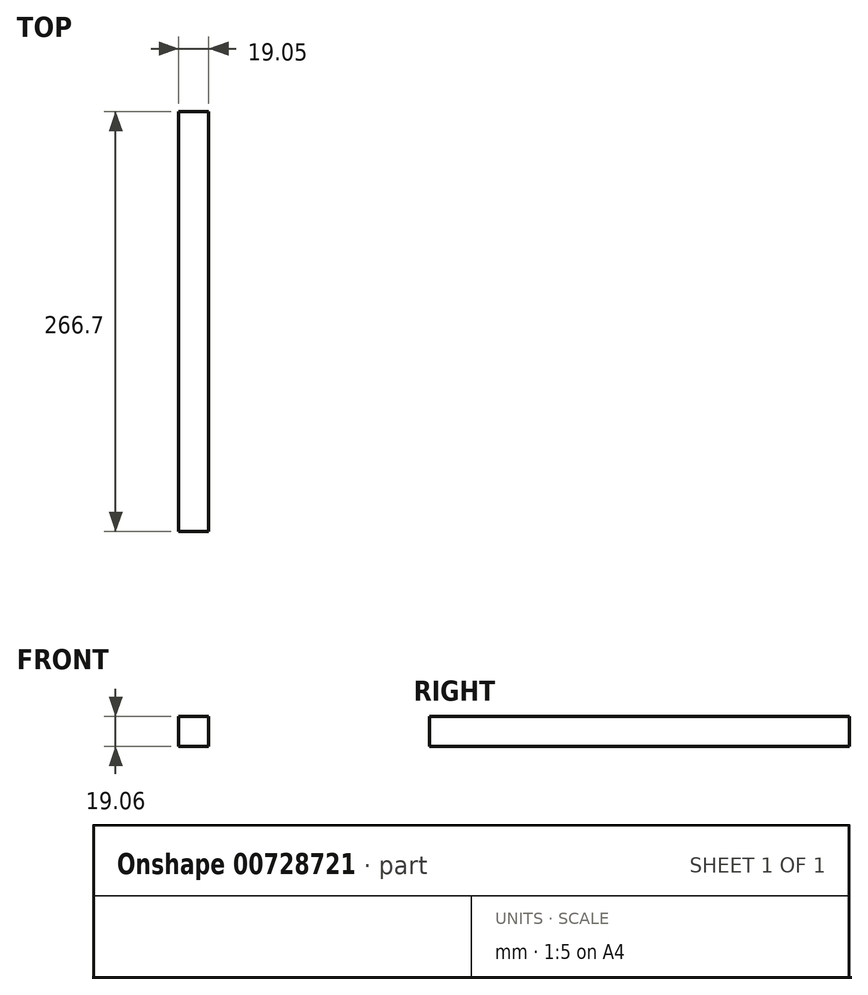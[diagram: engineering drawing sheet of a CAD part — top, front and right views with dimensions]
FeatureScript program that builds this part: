
annotation { "Feature Type Name" : "Feature", "Feature Type Description" : "" }
export const myFeature = defineFeature(function(context is Context, id is Id, definition is map)
    precondition{}
    {
        {
            var Q0;
            Q0=qCreatedBy(makeId("Right.planeOp"),FACE);
            var sketch = newSketch(context, id + "F0", { "sketchPlane" : qUnion([Q0])});
            skLineSegment(sketch, "E0.bottom", {"start": v(133.35, 9.53) * mm, "end": v(-133.35, 9.53) * mm});
            skLineSegment(sketch, "E0.top", {"start": v(133.35, -9.53) * mm, "end": v(-133.35, -9.53) * mm});
            skLineSegment(sketch, "E0.left", {"start": v(133.35, 9.53) * mm, "end": v(133.35, -9.53) * mm});
            skLineSegment(sketch, "E0.right", {"start": v(-133.35, 9.53) * mm, "end": v(-133.35, -9.53) * mm});
            skPoint(sketch, "E0.middle", {"position": v(0, 0) * mm});
            skSolve(sketch);
        }
        {
            var Q0;
            Q0 = qSketchRegion(id + "F0", true);
            extrude(context, id + "F1", {"entities" : qUnion([Q0]), "depth" : 19.05 * mm, "offsetDistance" : 25.4 * mm});
        }
    });
